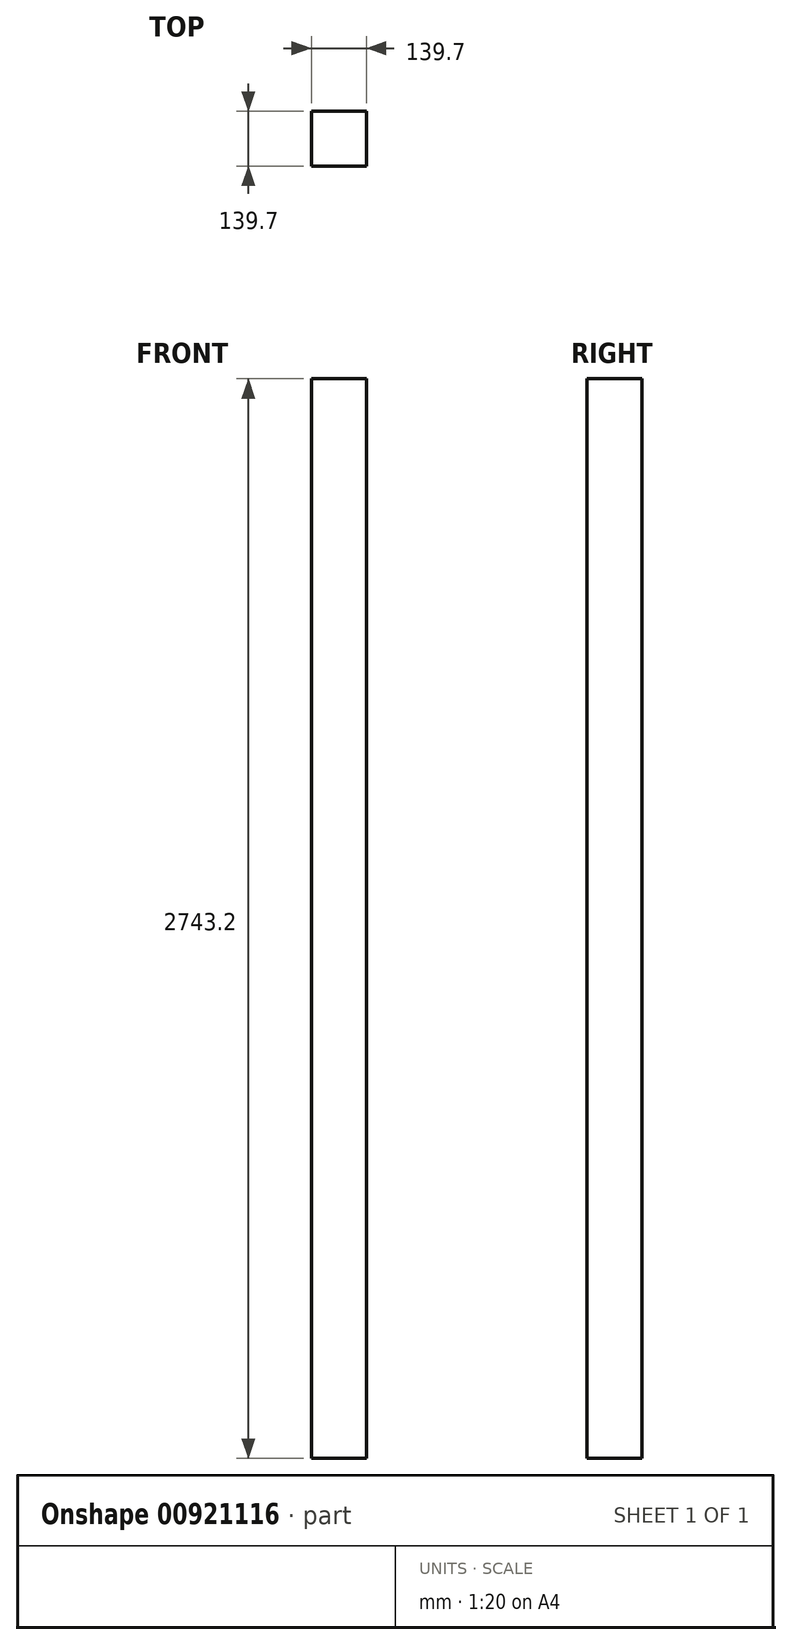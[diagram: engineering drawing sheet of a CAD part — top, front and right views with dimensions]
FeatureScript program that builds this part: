
annotation { "Feature Type Name" : "Feature", "Feature Type Description" : "" }
export const myFeature = defineFeature(function(context is Context, id is Id, definition is map)
    precondition{}
    {
        {
            var Q0;
            Q0=qCreatedBy(makeId("Top.planeOp"),FACE);
            var sketch = newSketch(context, id + "F0", { "sketchPlane" : qUnion([Q0])});
            skLineSegment(sketch, "E0.bottom", {"start": v(0, 40.07) * mm, "end": v(139.7, 40.07) * mm});
            skLineSegment(sketch, "E0.top", {"start": v(0, -99.63) * mm, "end": v(139.7, -99.63) * mm});
            skLineSegment(sketch, "E0.left", {"start": v(0, 40.07) * mm, "end": v(0, -99.63) * mm});
            skLineSegment(sketch, "E0.right", {"start": v(139.7, 40.07) * mm, "end": v(139.7, -99.63) * mm});
            skSolve(sketch);
        }
        {
            var Q0;
            Q0=qSketchRegion(id+"F0",true);
            extrude(context, id + "F1", {"entities" : qUnion([Q0]), "depth" : 2743.2 * mm, "offsetDistance" : 25.4 * mm});
        }
    });
